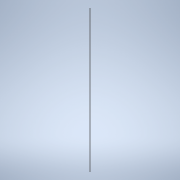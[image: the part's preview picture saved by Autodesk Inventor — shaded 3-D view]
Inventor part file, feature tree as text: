
AUTODESK INVENTOR PART (.ipt)
format: ipt  version: 2021.3 (Build 253353010, 353A)  size: 93,184 bytes
history: native  units: mm
features: extrude x1, sketch x1
ambient origin geometry x8: Origin, YZ Plane, XZ Plane, XY Plane, X Axis, Y Axis, Z Axis, Center Point
bodies: Solid1 (feature_tree)
feature tree (2):
  extrude  "Extrusion1"  Depth=2.0mm
  sketch  "Sketch1"  dims[d0=2.0mm d1=2.0mm d2=1000.0mm d3=0.0mm]
